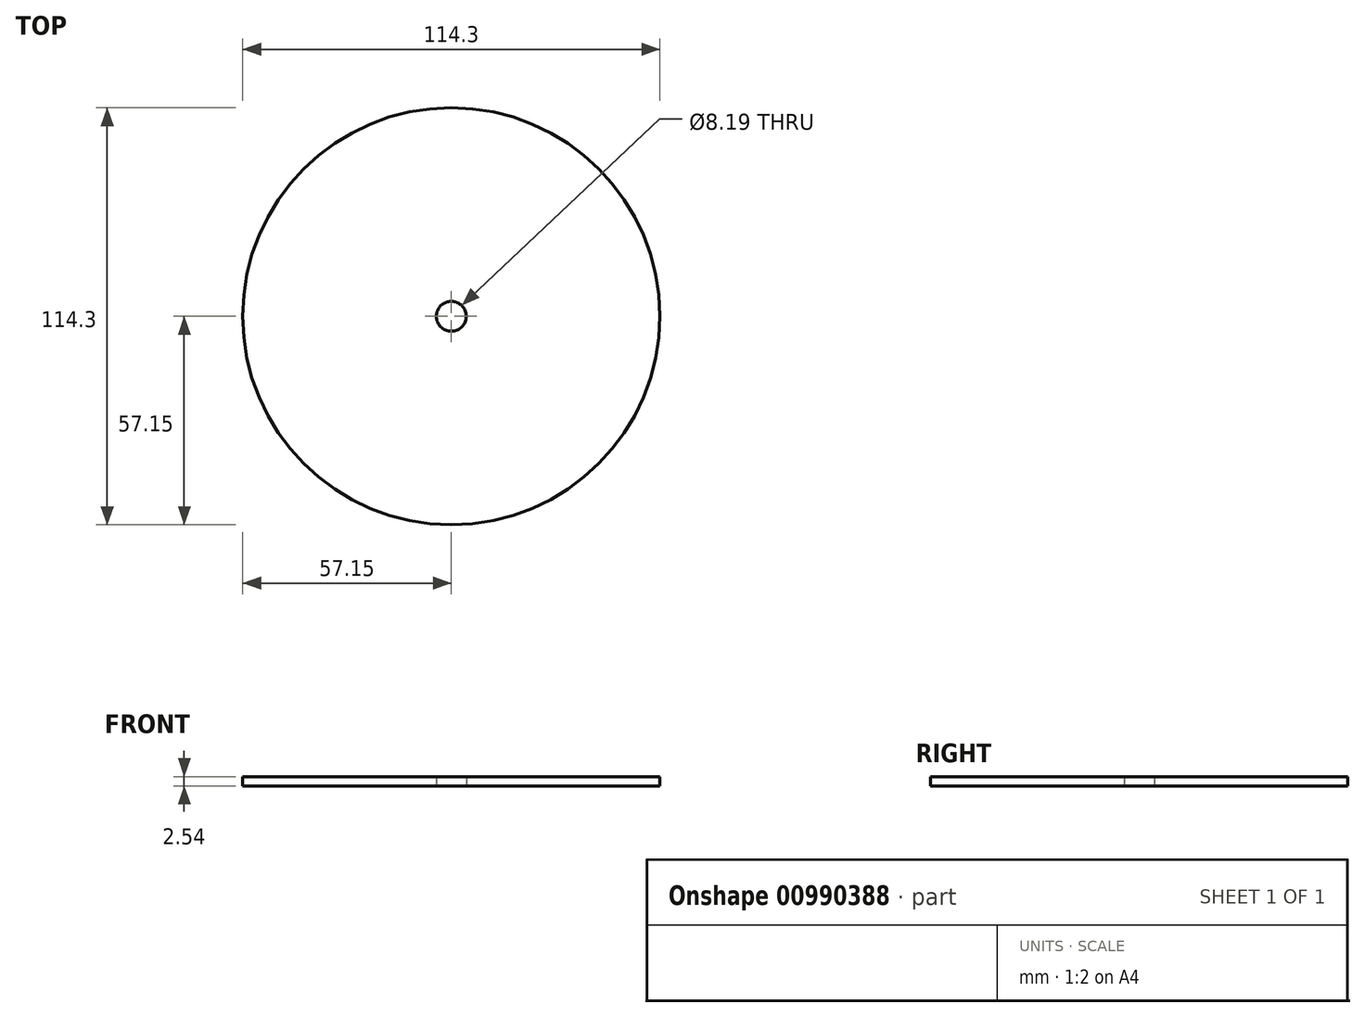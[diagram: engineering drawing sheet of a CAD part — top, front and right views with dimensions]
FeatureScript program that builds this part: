
annotation { "Feature Type Name" : "Feature", "Feature Type Description" : "" }
export const myFeature = defineFeature(function(context is Context, id is Id, definition is map)
    precondition{}
    {
        {
            var Q0;
            Q0=qCreatedBy(makeId("Top.planeOp"),FACE);
            var sketch = newSketch(context, id + "F0", { "sketchPlane" : qUnion([Q0])});
            skCircle(sketch, "E0", {"center": v(0, 0) * mm, "radius": 57.15 * mm});
            skSolve(sketch);
        }
        {
            var Q0;
            Q0=makeQuery(id+"F0.imprint","IMPRINT",FACE,{"disambiguationData":[TD([[makeQuery(id+"F0.imprint","IMPRINT",EDGE,{"derivedFrom":sQuery(id+"F0.wireOp",EDGE,"E0")}),1.0]])]});
            extrude(context, id + "F1", {"entities" : qUnion([Q0]), "depth" : 2.54 * mm, "offsetDistance" : 25.4 * mm});
        }
        {
            var Q0;
            Q0=qCreatedBy(makeId("Top.planeOp"),FACE);
            var sketch = newSketch(context, id + "F2", { "sketchPlane" : qUnion([Q0])});
            skCircle(sketch, "E1", {"center": v(0, 0) * mm, "radius": 4.1 * mm});
            skSolve(sketch);
        }
        {
            var Q0;
            Q0=makeQuery(id+"F2.imprint","IMPRINT",FACE,{"disambiguationData":[TD([[makeQuery(id+"F2.imprint","IMPRINT",EDGE,{"derivedFrom":sQuery(id+"F2.wireOp",EDGE,"E1")}),1.0]])]});
            var Q1;
            Q1=sQuery(id+"F2.wireOp",EDGE,"E1");
            extrude(context, id + "F3", {"entities" : qUnion([Q0]), "operationType" : NewBodyOperationType.REMOVE, "surfaceEntities" : qUnion([Q1]), "oppositeDirection" : true, "depth" : 25.4 * mm, "offsetDistance" : 25.4 * mm});
        }
        {
            var Q0;
            Q0=makeQuery(id+"F2.imprint","IMPRINT",FACE,{"disambiguationData":[TD([[makeQuery(id+"F2.imprint","IMPRINT",EDGE,{"derivedFrom":sQuery(id+"F2.wireOp",EDGE,"E1")}),1.0]])]});
            extrude(context, id + "F4", {"entities" : qUnion([Q0]), "operationType" : NewBodyOperationType.REMOVE, "depth" : 25.4 * mm, "offsetDistance" : 25.4 * mm});
        }
    });
